# Revit family: MRITH
name_source: partatom
category: Lighting Fixtures
units: mm (PartAtom-declared; Revit-internal decimal feet)

## family parameters
Cut with Voids When Loaded = No
Host = Face
Light Source = Yes
Maintain Annotation Orientation = No
Part Type = Normal
Room Calculation Point = No
Round Connector Dimension = Use Diameter
Shared = No

## types (13) — shared parameters
Assembly Code = D5020200
Color Filter = 16777215
Default Elevation = 4' - 0"
Description = Non-Ferrous MRI Recessed Architectural LED Luminaire
Dimming Lamp Color Temperature Shift = <None>
Emit Shape Visible in Rendering = No
Housing Finish = Metal - Viscor - White
Lamp = LED
Lens Finish = Acrylic - Viscor - Frosted Round
Manufacturer = CERTOLUX by VISCOR
Model = MRITH
Tilt Angle = -90.00°
URL = https://viscor.com
Voltage = 120 V

## per-type parameters (varying)
| type | Apparent Load | Cover Width | Emit from Rectangle Length | Emit from Rectangle Width | Lamp Wattage | Length | Photometric Web File | Width |
| MRITH1x4-LED840K040LUNV | 28 VA | 0' - 5 7/8" | 3' - 11 3/4" | 0' - 11 3/4" | 28 VA | 3' - 11 3/4" | MRITH1x4-LED840K040LUNV.IES | 0' - 11 3/4" |
| MRITH2X2-LED840K020LUNV | 13 VA | 0' - 11 7/8" | 1' - 11 3/4" | 1' - 11 3/4" | 13 VA | 1' - 11 3/4" | MRITH2X2-LED840K020LUNV.ies | 1' - 11 3/4" |
| MRITH2X2-LED840K032LUNV | 22 VA | 0' - 11 7/8" | 1' - 11 3/4" | 1' - 11 3/4" | 22 VA | 1' - 11 3/4" | MRITH2X2-LED840K032LUNV.ies | 1' - 11 3/4" |
| MRITH2x4-LED840K040LUNV | 28 VA | 0' - 11 7/8" | 3' - 11 3/4" | 1' - 11 3/4" | 28 VA | 3' - 11 3/4" | MRITH2x4-LED840K040LUNV.IES | 1' - 11 3/4" |
| MRITH2x4-LED840K050LUNV | 35 VA | 0' - 11 7/8" | 3' - 11 3/4" | 1' - 11 3/4" | 35 VA | 3' - 11 3/4" | MRITH2x4-LED840K050LUNV.IES | 1' - 11 3/4" |
| MRITH1X4-LED840K020LUNV | 13 VA | 0' - 5 7/8" | 3' - 11 3/4" | 0' - 11 3/4" | 13 VA | 3' - 11 3/4" | MRITH1X4-LED840K020LUNV.ies | 0' - 11 3/4" |
| MRITH1X4-LED840K047LUNV | 35 VA | 0' - 5 7/8" | 3' - 11 3/4" | 0' - 11 3/4" | 35 VA | 3' - 11 3/4" | MRITH1X4-LED840K047LUNV.ies | 0' - 11 3/4" |
| MRITH1X4-LED840K050LUNV | 37 VA | 0' - 5 7/8" | 3' - 11 3/4" | 0' - 11 3/4" | 37 VA | 3' - 11 3/4" | MRITH1X4-LED840K050LUNV.ies | 0' - 11 3/4" |
| MRITH2X2-LED840K037LUNV | 25 VA | 0' - 11 7/8" | 1' - 11 3/4" | 1' - 11 3/4" | 25 VA | 1' - 11 3/4" | MRITH2X2-LED840K037LUNV.ies | 1' - 11 3/4" |
| MRITH2X2-LED840K040LUNV | 28 VA | 0' - 11 7/8" | 1' - 11 3/4" | 1' - 11 3/4" | 28 VA | 1' - 11 3/4" | MRITH2X2-LED840K040LUNV.ies | 1' - 11 3/4" |
| MRITH2X2-LED840K050LUNV | 36 VA | 0' - 11 7/8" | 1' - 11 3/4" | 1' - 11 3/4" | 36 VA | 1' - 11 3/4" | MRITH2X2-LED840K050LUNV.ies | 1' - 11 3/4" |
| MRITH2X4-LED840K072LUNV | 50 VA | 0' - 11 7/8" | 3' - 11 3/4" | 1' - 11 3/4" | 50 VA | 3' - 11 3/4" | MRITH2X4-LED840K072LUNV.ies | 1' - 11 3/4" |
| MRITH2X4-LED840K080LUNV | 57 VA | 0' - 11 7/8" | 3' - 11 3/4" | 1' - 11 3/4" | 57 VA | 3' - 11 3/4" | MRITH2X4-LED840K080LUNV.ies | 1' - 11 3/4" |

## geometry (parser evidence)
native form markers: Sweep x4
no freeform markers — native parametric forms only
